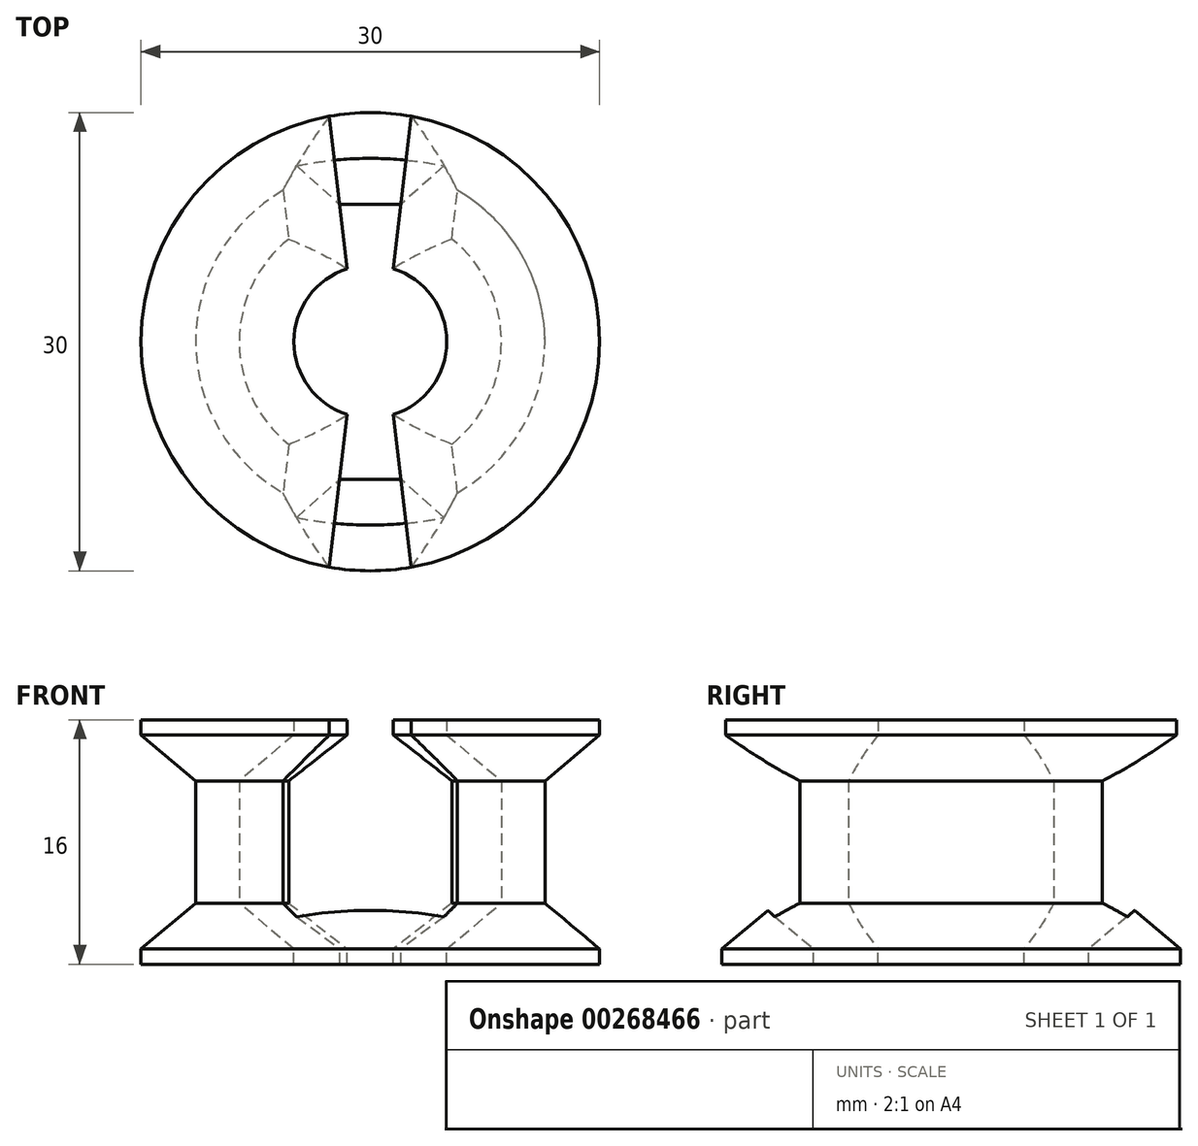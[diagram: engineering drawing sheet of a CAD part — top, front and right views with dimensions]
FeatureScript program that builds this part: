
annotation { "Feature Type Name" : "Feature", "Feature Type Description" : "" }
export const myFeature = defineFeature(function(context is Context, id is Id, definition is map)
    precondition{}
    {
        {
            var Q0;
            Q0=qCreatedBy(makeId("Top.planeOp"),FACE);
            var sketch = newSketch(context, id + "F0", { "sketchPlane" : qUnion([Q0])});
            skCircle(sketch, "E0", {"center": v(0, 0) * mm, "radius": 5 * mm});
            skCircle(sketch, "E1", {"center": v(0, 0) * mm, "radius": 15 * mm});
            skLineSegment(sketch, "E2", {"start": v(-1.5, 4.77) * mm, "end": v(-2, 9) * mm});
            skLineSegment(sketch, "E3", {"start": v(-2, 9) * mm, "end": v(2, 9) * mm});
            skLineSegment(sketch, "E4", {"start": v(2, 9) * mm, "end": v(1.5, 4.77) * mm});
            skLineSegment(sketch, "E5", {"start": v(-1.5, -4.77) * mm, "end": v(-2, -9) * mm});
            skLineSegment(sketch, "E6", {"start": v(-2, -9) * mm, "end": v(2, -9) * mm});
            skLineSegment(sketch, "E7", {"start": v(2, -9) * mm, "end": v(1.5, -4.77) * mm});
            skSolve(sketch);
        }
        {
            var Q0;
            Q0=makeQuery(id+"F0.imprint","IMPRINT",FACE,{"disambiguationData":[TD([[makeQuery(id+"F0.imprint","IMPRINT",EDGE,{"derivedFrom":sQuery(id+"F0.wireOp",EDGE,"E1")}),1.0]])]});
            extrude(context, id + "F1", {"entities" : qUnion([Q0]), "depth" : 3 * mm, "hasDraft" : true, "draftAngle" : 50 * degree, "draftPullDirection" : true});
        }
        {
            var Q0;
            Q0=makeQuery(id+"F1.opExtrude","CAP_FACE",FACE,{"disambiguationData":[OSD([sQuery(id+"F0.wireOp",EDGE,"E0"),sQuery(id+"F0.wireOp",EDGE,"E1"),sQuery(id+"F0.wireOp",EDGE,"E2"),sQuery(id+"F0.wireOp",EDGE,"E4"),sQuery(id+"F0.wireOp",EDGE,"E3"),sQuery(id+"F0.wireOp",EDGE,"E5"),sQuery(id+"F0.wireOp",EDGE,"E6"),sQuery(id+"F0.wireOp",EDGE,"E7")])],"isStart":false});
            extrude(context, id + "F2", {"entities" : qUnion([Q0]), "operationType" : NewBodyOperationType.ADD, "depth" : 8 * mm});
        }
        {
            var Q0;
            Q0=makeQuery(id+"F2.opExtrude","CAP_FACE",FACE,{"disambiguationData":[OSD([sQuery(id+"F0.wireOp",EDGE,"E0"),sQuery(id+"F0.wireOp",EDGE,"E1"),sQuery(id+"F0.wireOp",EDGE,"E2"),sQuery(id+"F0.wireOp",EDGE,"E4"),sQuery(id+"F0.wireOp",EDGE,"E3"),sQuery(id+"F0.wireOp",EDGE,"E5"),sQuery(id+"F0.wireOp",EDGE,"E6"),sQuery(id+"F0.wireOp",EDGE,"E7")])],"isStart":false});
            extrude(context, id + "F3", {"entities" : qUnion([Q0]), "operationType" : NewBodyOperationType.ADD, "depth" : 3 * mm, "hasDraft" : true, "draftAngle" : 50 * degree});
        }
        {
            var Q0;
            Q0=makeQuery(id+"F1.opExtrude","CAP_FACE",FACE,{"disambiguationData":[OSD([sQuery(id+"F0.wireOp",EDGE,"E0"),sQuery(id+"F0.wireOp",EDGE,"E1"),sQuery(id+"F0.wireOp",EDGE,"E2"),sQuery(id+"F0.wireOp",EDGE,"E4"),sQuery(id+"F0.wireOp",EDGE,"E3"),sQuery(id+"F0.wireOp",EDGE,"E5"),sQuery(id+"F0.wireOp",EDGE,"E6"),sQuery(id+"F0.wireOp",EDGE,"E7")])],"isStart":true});
            extrude(context, id + "F4", {"entities" : qUnion([Q0]), "operationType" : NewBodyOperationType.ADD, "depth" : 1 * mm});
        }
        {
            var Q0;
            {var subQ0=sQuery(id+"F0.wireOp",EDGE,"E7");var subQ1=sQuery(id+"F0.wireOp",EDGE,"E6");var subQ2=sQuery(id+"F0.wireOp",EDGE,"E5");var subQ3=sQuery(id+"F0.wireOp",EDGE,"E3");var subQ4=sQuery(id+"F0.wireOp",EDGE,"E4");var subQ5=sQuery(id+"F0.wireOp",EDGE,"E2");var subQ6=sQuery(id+"F0.wireOp",EDGE,"E1");var subQ7=sQuery(id+"F0.wireOp",EDGE,"E0");Q0=makeQuery(id+"F3.opExtrude","CAP_FACE",FACE,{"disambiguationData":[OSD([subQ7,subQ6,subQ5,subQ4,subQ3,subQ2,subQ1,subQ0]),TDD([makeQuery(id+"F2.opExtrude","CAP_FACE",FACE,{"disambiguationData":[OSD([subQ7,subQ6,subQ5,subQ4,subQ3,subQ2,subQ1,subQ0]),TDD([makeQuery(id+"F1.*.draft.opDraft","SPLIT",FACE,{"disambiguationData":[OD(1.0)],"derivedFrom":makeQuery(id+"F1.opExtrude","CAP_FACE",FACE,{"disambiguationData":[OSD([subQ7,subQ6,subQ5,subQ4,subQ3,subQ2,subQ1,subQ0])],"isStart":false})})])],"isStart":false})])],"isStart":false});}
            var Q1;
            {var subQ0=sQuery(id+"F0.wireOp",EDGE,"E7");var subQ1=sQuery(id+"F0.wireOp",EDGE,"E6");var subQ2=sQuery(id+"F0.wireOp",EDGE,"E5");var subQ3=sQuery(id+"F0.wireOp",EDGE,"E3");var subQ4=sQuery(id+"F0.wireOp",EDGE,"E4");var subQ5=sQuery(id+"F0.wireOp",EDGE,"E2");var subQ6=sQuery(id+"F0.wireOp",EDGE,"E1");var subQ7=sQuery(id+"F0.wireOp",EDGE,"E0");Q1=makeQuery(id+"F3.opExtrude","CAP_FACE",FACE,{"disambiguationData":[OSD([subQ7,subQ6,subQ5,subQ4,subQ3,subQ2,subQ1,subQ0]),TDD([makeQuery(id+"F2.opExtrude","CAP_FACE",FACE,{"disambiguationData":[OSD([subQ7,subQ6,subQ5,subQ4,subQ3,subQ2,subQ1,subQ0]),TDD([makeQuery(id+"F1.*.draft.opDraft","SPLIT",FACE,{"disambiguationData":[OD(0.0)],"derivedFrom":makeQuery(id+"F1.opExtrude","CAP_FACE",FACE,{"disambiguationData":[OSD([subQ7,subQ6,subQ5,subQ4,subQ3,subQ2,subQ1,subQ0])],"isStart":false})})])],"isStart":false})])],"isStart":false});}
            extrude(context, id + "F5", {"entities" : qUnion([Q0, Q1]), "operationType" : NewBodyOperationType.ADD, "depth" : 1 * mm});
        }
    });
